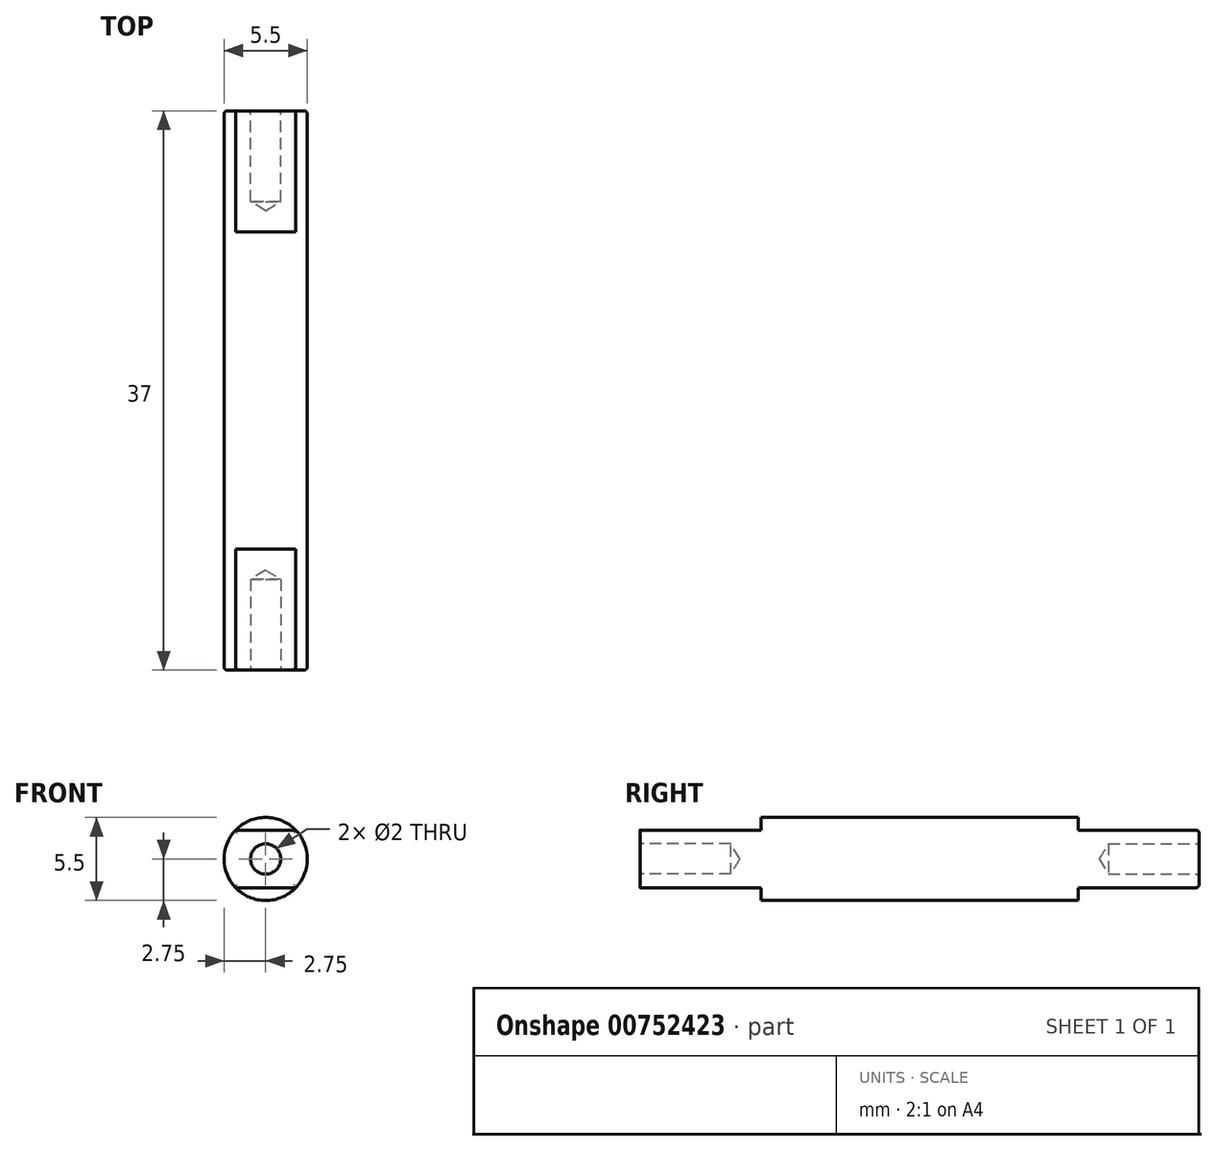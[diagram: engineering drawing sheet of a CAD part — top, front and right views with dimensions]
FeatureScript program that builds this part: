
annotation { "Feature Type Name" : "Feature", "Feature Type Description" : "" }
export const myFeature = defineFeature(function(context is Context, id is Id, definition is map)
    precondition{}
    {
        {
            var Q0;
            Q0=qCreatedBy(makeId("Front.planeOp"),FACE);
            var sketch = newSketch(context, id + "F0", { "sketchPlane" : qUnion([Q0])});
            skCircle(sketch, "E0", {"center": v(0, 0) * mm, "radius": 2.75 * mm});
            skSolve(sketch);
        }
        {
            var Q0;
            Q0=makeQuery(id+"F0.imprint","IMPRINT",FACE,{"disambiguationData":[TD([[makeQuery(id+"F0.imprint","IMPRINT",EDGE,{"derivedFrom":sQuery(id+"F0.wireOp",EDGE,"E0")}),1.0]])]});
            extrude(context, id + "F1", {"entities" : qUnion([Q0]), "endBound" : BoundingType.SYMMETRIC, "depth" : 37 * mm, "offsetDistance" : 25 * mm});
        }
        {
            var Q0;
            Q0=makeQuery(id+"F1.opExtrude","CAP_FACE",FACE,{"disambiguationData":[OSD([sQuery(id+"F0.wireOp",EDGE,"E0")])],"isStart":false});
            var sketch = newSketch(context, id + "F2", { "sketchPlane" : qUnion([Q0])});
            skLineSegment(sketch, "E1.bottom", {"start": v(-1.99, 2.75) * mm, "end": v(1.99, 2.75) * mm});
            skLineSegment(sketch, "E1.top", {"start": v(-1.99, 1.9) * mm, "end": v(1.99, 1.9) * mm});
            skLineSegment(sketch, "E1.left", {"start": v(-1.99, 2.75) * mm, "end": v(-1.99, 1.9) * mm});
            skLineSegment(sketch, "E1.right", {"start": v(1.99, 2.75) * mm, "end": v(1.99, 1.9) * mm});
            skPoint(sketch, "E1.middle", {"position": v(0, 2.33) * mm});
            skLineSegment(sketch, "E2.MirrorCS", {"start": v(-1.99, -1.9) * mm, "end": v(1.99, -1.9) * mm});
            skLineSegment(sketch, "E3.MirrorCS", {"start": v(-1.99, -2.75) * mm, "end": v(-1.99, -1.9) * mm});
            skLineSegment(sketch, "E4.MirrorCS", {"start": v(-1.99, -2.75) * mm, "end": v(1.99, -2.75) * mm});
            skLineSegment(sketch, "E5.MirrorCS", {"start": v(1.99, -2.75) * mm, "end": v(1.99, -1.9) * mm});
            skSolve(sketch);
        }
        {
            var Q0;
            {var subQ0=sQuery(id+"F2.wireOp",EDGE,"E1.top");Q0=makeQuery(id+"F2.imprint","IMPRINT",FACE,{"disambiguationData":[TD([[makeQuery(id+"F2.imprint","IMPRINT",EDGE,{"derivedFrom":subQ0}),1.0]])]});}
            var Q1;
            {var subQ0=sQuery(id+"F2.wireOp",EDGE,"E2.MirrorCS");Q1=makeQuery(id+"F2.imprint","IMPRINT",FACE,{"disambiguationData":[TD([[makeQuery(id+"F2.imprint","IMPRINT",EDGE,{"derivedFrom":subQ0}),-1.0]])]});}
            extrude(context, id + "F3", {"entities" : qUnion([Q0, Q1]), "operationType" : NewBodyOperationType.REMOVE, "oppositeDirection" : true, "depth" : 8 * mm, "offsetDistance" : 25 * mm});
        }
        {
            var Q0;
            Q0=makeQuery(id+"F1.opExtrude","SWEPT_BODY",BODY,{"disambiguationData":[OSD([sQuery(id+"F0.wireOp",EDGE,"E0")])]});
            var Q1;
            Q1=qCreatedBy(makeId("Front.planeOp"),FACE);
            mirror(context, id + "F4", {"operationType" : NewBodyOperationType.INTERSECT, "entities" : qUnion([Q0]), "mirrorPlane" : qUnion([Q1])});
        }
        {
            var Q0;
            Q0=makeQuery(id+"F1.opExtrude","CAP_FACE",FACE,{"disambiguationData":[OSD([sQuery(id+"F0.wireOp",EDGE,"E0")])],"isStart":false});
            var sketch = newSketch(context, id + "F5", { "sketchPlane" : qUnion([Q0])});
            skPoint(sketch, "E6", {"position": v(0, 0) * mm});
            skSolve(sketch);
        }
        {
            var Q0;
            Q0=makeQuery(id+"F1.opExtrude","CAP_FACE",FACE,{"disambiguationData":[OSD([sQuery(id+"F0.wireOp",EDGE,"E0")])],"isStart":true});
            var sketch = newSketch(context, id + "F6", { "sketchPlane" : qUnion([Q0])});
            skPoint(sketch, "E7", {"position": v(0, 0) * mm});
            skSolve(sketch);
        }
        {
            var Q0;
            Q0=sQuery(id+"F6.wireOp",VERTEX,"E7");
            var Q1;
            Q1=sQuery(id+"F5.wireOp",VERTEX,"E6");
            var Q2;
            Q2=makeQuery(id+"F1.opExtrude","SWEPT_BODY",BODY,{"disambiguationData":[OSD([sQuery(id+"F0.wireOp",EDGE,"E0")])]});
            hole(context, id + "F7", {"style" : HoleStyle.SIMPLE, "endStyle" : HoleEndStyle.BLIND, "holeDiameter" : 2 * mm, "majorDiameter" : 5 * mm, "holeDepth" : 6 * mm, "isTappedThrough" : true, "tappedDepth" : 12 * mm, "tapClearance" : 3, "locations" : qUnion([Q0, Q1]), "scope" : qUnion([Q2])});
        }
        {
            var Q0;
            Q0=makeQuery(id+"F3.boolean.opBoolean","SPLIT",EDGE,{"disambiguationData":[OD(0.0)],"derivedFrom":makeQuery(id+"F1.opExtrude","CAP_EDGE",EDGE,{"disambiguationData":[OSD([sQuery(id+"F0.wireOp",EDGE,"E0")])],"isStart":false})});
            var Q1;
            Q1=makeQuery(id+"F7.hole-1.boolean.opBoolean","COPY",EDGE,{"derivedFrom":makeQuery(id+"F7.hole-1.opRevolve","SWEPT_EDGE",EDGE,{"disambiguationData":[OSD([sQuery(id+"F7.hole-1.sketch.wireOp",EDGE,"core_line_2"),sQuery(id+"F7.hole-1.sketch.wireOp",EDGE,"core_line_3")])]})});
            var Q2;
            Q2=makeQuery(id+"F3.boolean.opBoolean","SPLIT",EDGE,{"disambiguationData":[OD(1.0)],"derivedFrom":makeQuery(id+"F1.opExtrude","CAP_EDGE",EDGE,{"disambiguationData":[OSD([sQuery(id+"F0.wireOp",EDGE,"E0")])],"isStart":false})});
            var Q3;
            Q3=makeQuery(id+"F3.boolean.opBoolean","COPY",EDGE,{"derivedFrom":makeQuery(id+"F3.opExtrude","SWEPT_EDGE",EDGE,{"disambiguationData":[OSD([sQuery(id+"F0.wireOp",EDGE,"E0"),sQuery(id+"F2.wireOp",EDGE,"E2.MirrorCS"),sQuery(id+"F2.wireOp",EDGE,"E3.MirrorCS")])]})});
            var Q4;
            Q4=makeQuery(id+"F3.boolean.opBoolean","COPY",EDGE,{"derivedFrom":makeQuery(id+"F3.opExtrude","SWEPT_EDGE",EDGE,{"disambiguationData":[OSD([sQuery(id+"F0.wireOp",EDGE,"E0"),sQuery(id+"F2.wireOp",EDGE,"E2.MirrorCS"),sQuery(id+"F2.wireOp",EDGE,"E5.MirrorCS")])]})});
            var Q5;
            Q5=makeQuery(id+"F3.boolean.opBoolean","COPY",EDGE,{"derivedFrom":makeQuery(id+"F3.opExtrude","SWEPT_EDGE",EDGE,{"disambiguationData":[OSD([sQuery(id+"F0.wireOp",EDGE,"E0"),sQuery(id+"F2.wireOp",EDGE,"E1.top"),sQuery(id+"F2.wireOp",EDGE,"E1.left")])]})});
            var Q6;
            Q6=makeQuery(id+"F3.boolean.opBoolean","COPY",EDGE,{"derivedFrom":makeQuery(id+"F3.opExtrude","CAP_EDGE",EDGE,{"disambiguationData":[OSD([sQuery(id+"F2.wireOp",EDGE,"E2.MirrorCS")])],"isStart":true})});
            var Q7;
            Q7=makeQuery(id+"F3.boolean.opBoolean","COPY",EDGE,{"derivedFrom":makeQuery(id+"F3.opExtrude","CAP_EDGE",EDGE,{"disambiguationData":[OSD([sQuery(id+"F2.wireOp",EDGE,"E1.top")])],"isStart":true})});
            var Q8;
            Q8=makeQuery(id+"F3.boolean.opBoolean","COPY",EDGE,{"derivedFrom":makeQuery(id+"F3.opExtrude","SWEPT_EDGE",EDGE,{"disambiguationData":[OSD([sQuery(id+"F0.wireOp",EDGE,"E0"),sQuery(id+"F2.wireOp",EDGE,"E1.top"),sQuery(id+"F2.wireOp",EDGE,"E1.right")])]})});
            var Q9;
            Q9=makeQuery(id+"F4.boolean.opBoolean","COPY",EDGE,{"derivedFrom":makeQuery(id+"F4.boolean.toolComplement.opBoolean","COPY",EDGE,{"derivedFrom":makeQuery(id+"F4.opPattern","COPY",EDGE,{"derivedFrom":makeQuery(id+"F3.boolean.opBoolean","COPY",EDGE,{"derivedFrom":makeQuery(id+"F3.opExtrude","SWEPT_EDGE",EDGE,{"disambiguationData":[OSD([sQuery(id+"F0.wireOp",EDGE,"E0"),sQuery(id+"F2.wireOp",EDGE,"E1.top"),sQuery(id+"F2.wireOp",EDGE,"E1.right")])]})}),"instanceName":"1"})})});
            var Q10;
            Q10=makeQuery(id+"F4.boolean.opBoolean","COPY",EDGE,{"derivedFrom":makeQuery(id+"F4.boolean.toolComplement.opBoolean","COPY",EDGE,{"derivedFrom":makeQuery(id+"F4.opPattern","COPY",EDGE,{"derivedFrom":makeQuery(id+"F3.boolean.opBoolean","COPY",EDGE,{"derivedFrom":makeQuery(id+"F3.opExtrude","SWEPT_EDGE",EDGE,{"disambiguationData":[OSD([sQuery(id+"F0.wireOp",EDGE,"E0"),sQuery(id+"F2.wireOp",EDGE,"E1.top"),sQuery(id+"F2.wireOp",EDGE,"E1.left")])]})}),"instanceName":"1"})})});
            var Q11;
            Q11=makeQuery(id+"F4.boolean.opBoolean","COPY",EDGE,{"derivedFrom":makeQuery(id+"F4.boolean.toolComplement.opBoolean","COPY",EDGE,{"derivedFrom":makeQuery(id+"F4.opPattern","COPY",EDGE,{"derivedFrom":makeQuery(id+"F3.boolean.opBoolean","COPY",EDGE,{"derivedFrom":makeQuery(id+"F3.opExtrude","SWEPT_EDGE",EDGE,{"disambiguationData":[OSD([sQuery(id+"F0.wireOp",EDGE,"E0"),sQuery(id+"F2.wireOp",EDGE,"E2.MirrorCS"),sQuery(id+"F2.wireOp",EDGE,"E3.MirrorCS")])]})}),"instanceName":"1"})})});
            var Q12;
            Q12=makeQuery(id+"F4.boolean.opBoolean","COPY",EDGE,{"derivedFrom":makeQuery(id+"F4.boolean.toolComplement.opBoolean","COPY",EDGE,{"derivedFrom":makeQuery(id+"F4.opPattern","COPY",EDGE,{"derivedFrom":makeQuery(id+"F3.boolean.opBoolean","COPY",EDGE,{"derivedFrom":makeQuery(id+"F3.opExtrude","SWEPT_EDGE",EDGE,{"disambiguationData":[OSD([sQuery(id+"F0.wireOp",EDGE,"E0"),sQuery(id+"F2.wireOp",EDGE,"E2.MirrorCS"),sQuery(id+"F2.wireOp",EDGE,"E5.MirrorCS")])]})}),"instanceName":"1"})})});
            var Q13;
            Q13=makeQuery(id+"F1.opExtrude","CAP_FACE",FACE,{"disambiguationData":[OSD([sQuery(id+"F0.wireOp",EDGE,"E0")])],"isStart":true});
            fillet(context, id + "F8", {"entities" : qUnion([Q0, Q1, Q2, Q3, Q4, Q5, Q6, Q7, Q8, Q9, Q10, Q11, Q12, Q13]), "radius" : 0.2 * mm, "tangentPropagation" : true, "allowEdgeOverflow" : false});
        }
    });
